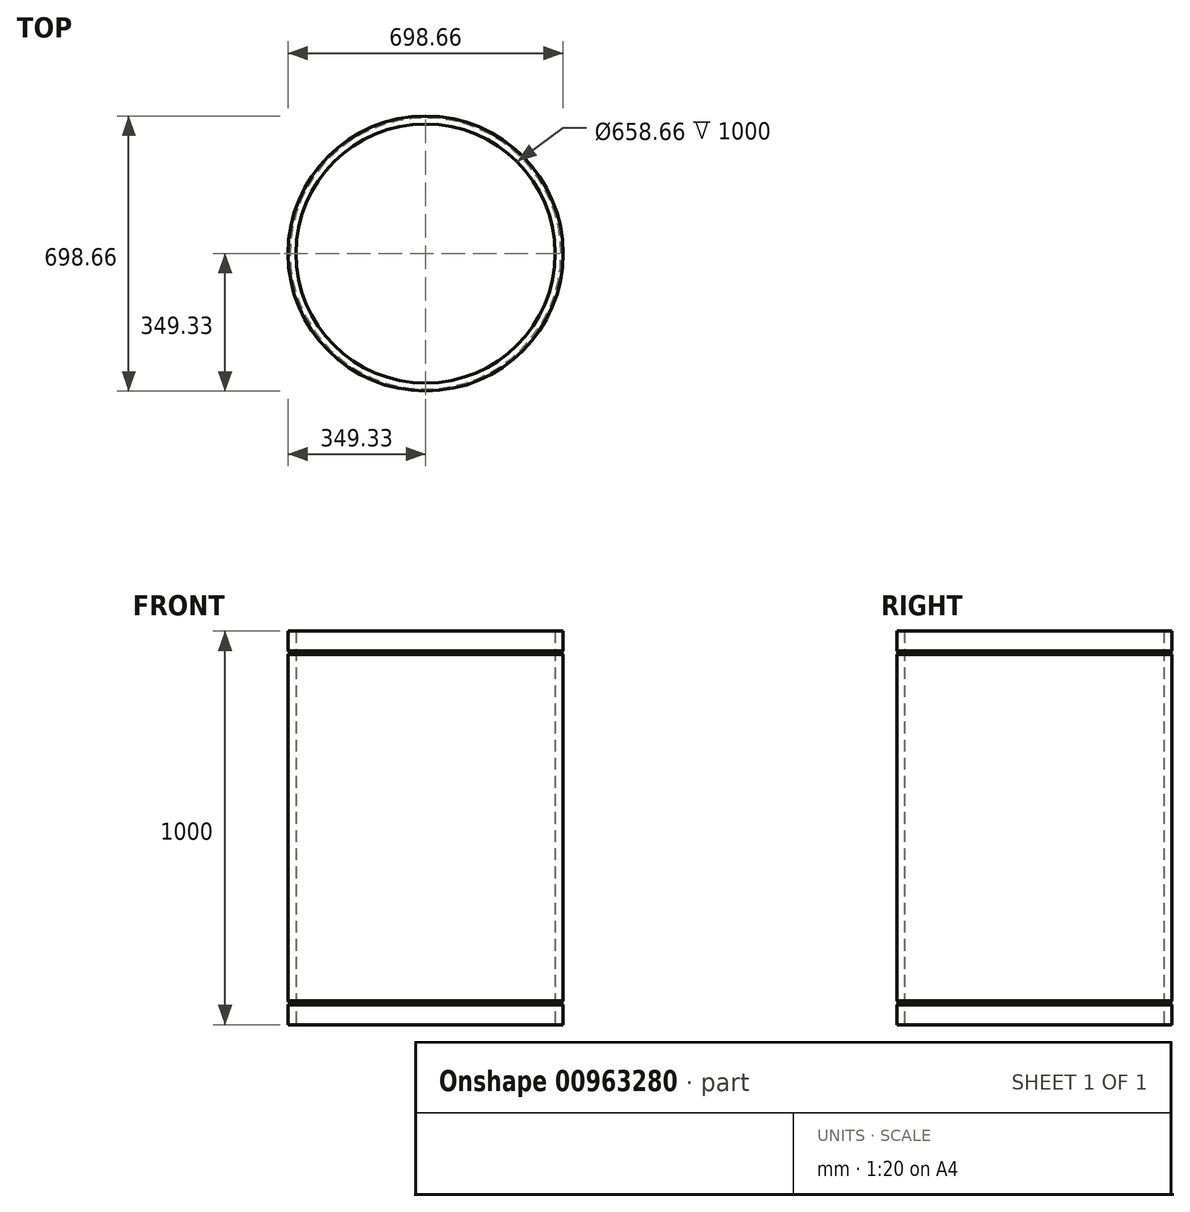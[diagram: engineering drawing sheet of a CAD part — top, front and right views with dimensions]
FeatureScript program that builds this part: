
annotation { "Feature Type Name" : "Feature", "Feature Type Description" : "" }
export const myFeature = defineFeature(function(context is Context, id is Id, definition is map)
    precondition{}
    {
        {
            var Q0;
            Q0=qCreatedBy(makeId("Front.planeOp"),FACE);
            var sketch = newSketch(context, id + "F0", { "sketchPlane" : qUnion([Q0])});
            skLineSegment(sketch, "E0", {"start": v(0, 0) * mm, "end": v(0, 1000) * mm, "construction": true});
            skLineSegment(sketch, "E1", {"start": v(-329.33, 0) * mm, "end": v(-329.33, 1000) * mm});
            skLineSegment(sketch, "E2", {"start": v(-329.33, 1000) * mm, "end": v(-349.33, 1000) * mm});
            skLineSegment(sketch, "E3", {"start": v(-349.33, 1000) * mm, "end": v(-349.33, 950) * mm});
            skLineSegment(sketch, "E4", {"start": v(-349.33, 950) * mm, "end": v(-344.33, 945) * mm});
            skLineSegment(sketch, "E5", {"start": v(-344.33, 945) * mm, "end": v(-349.33, 940) * mm});
            skLineSegment(sketch, "E6", {"start": v(-349.33, 940) * mm, "end": v(-349.33, 60) * mm});
            skLineSegment(sketch, "E7", {"start": v(-349.33, 60) * mm, "end": v(-344.33, 55) * mm});
            skLineSegment(sketch, "E8", {"start": v(-344.33, 55) * mm, "end": v(-349.33, 50) * mm});
            skLineSegment(sketch, "E9", {"start": v(-349.33, 50) * mm, "end": v(-349.33, 0) * mm});
            skLineSegment(sketch, "E10", {"start": v(-349.33, 0) * mm, "end": v(-329.33, 0) * mm});
            skSolve(sketch);
        }
        {
            var Q0;
            Q0=makeQuery(id+"F0.imprint","IMPRINT",FACE,{"disambiguationData":[TD([[makeQuery(id+"F0.imprint","IMPRINT",EDGE,{"derivedFrom":sQuery(id+"F0.wireOp",EDGE,"E1")}),1.0]])]});
            var Q1;
            Q1=sQuery(id+"F0.wireOp",EDGE,"E0");
            revolve(context, id + "F1", {"surfaceOperationType" : NewSurfaceOperationType.NEW, "entities" : qUnion([Q0]), "axis" : qUnion([Q1]), "revolveType" : RevolveType.FULL});
        }
    });
